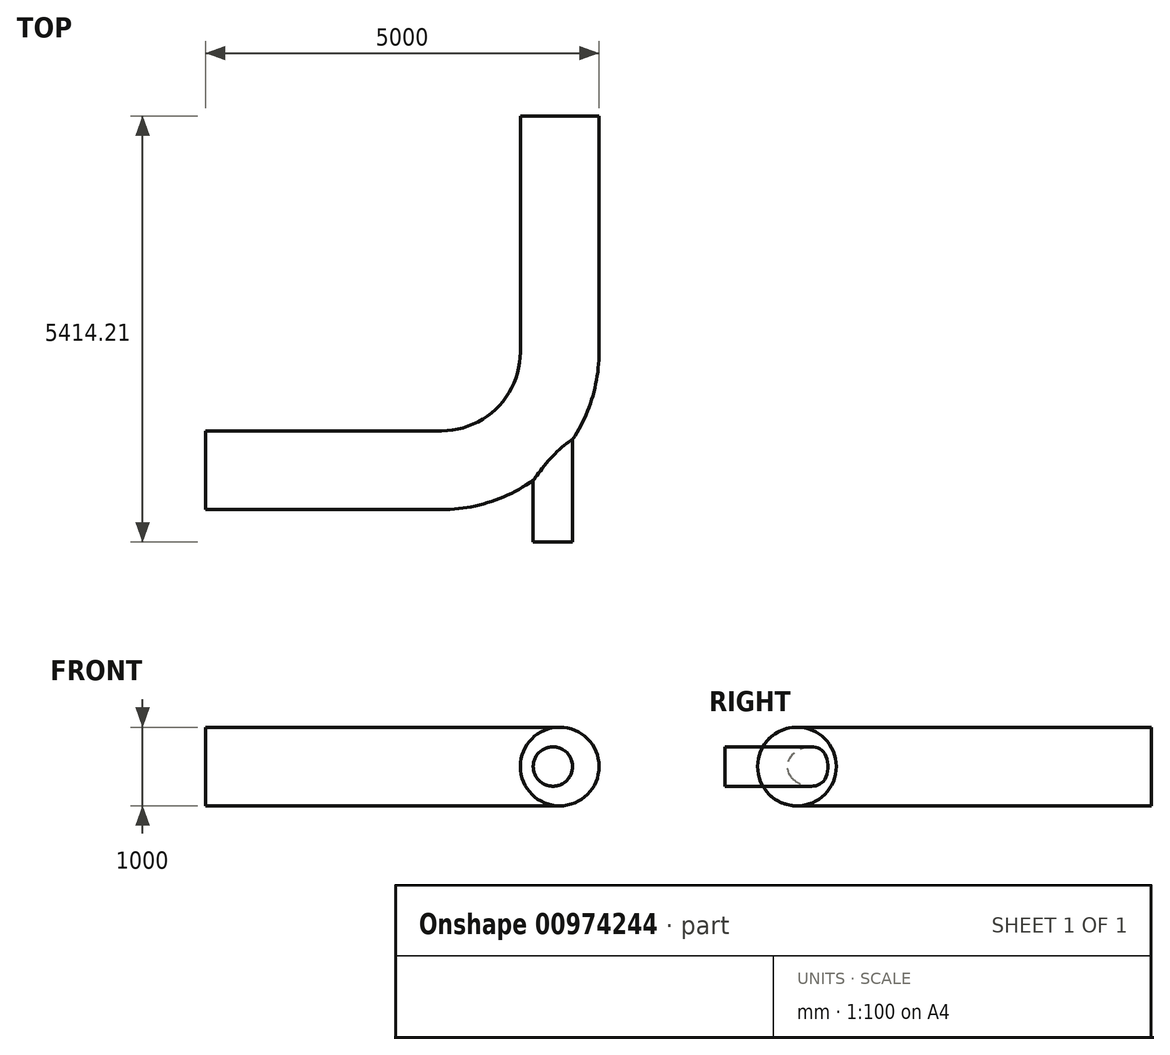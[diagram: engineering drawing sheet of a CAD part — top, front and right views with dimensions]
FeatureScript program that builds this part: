
annotation { "Feature Type Name" : "Feature", "Feature Type Description" : "" }
export const myFeature = defineFeature(function(context is Context, id is Id, definition is map)
    precondition{}
    {
        {
            var Q0;
            Q0=qCreatedBy(makeId("Top.planeOp"),FACE);
            var sketch = newSketch(context, id + "F0", { "sketchPlane" : qUnion([Q0])});
            skLineSegment(sketch, "E0", {"start": v(0, 0) * mm, "end": v(3000, 0) * mm});
            skArc(sketch, "E1", {"start": v(3000, 0) * mm, "mid": v(4060.66, 439.34) * mm, "end": v(4500, 1500) * mm});
            skLineSegment(sketch, "E2", {"start": v(4500, 1500) * mm, "end": v(4500, 4500) * mm});
            skLineSegment(sketch, "E3", {"start": v(3000, 0) * mm, "end": v(3000, 1500) * mm, "construction": true});
            skLineSegment(sketch, "E4", {"start": v(4500, 1500) * mm, "end": v(3000, 1500) * mm, "construction": true});
            skLineSegment(sketch, "E5", {"start": v(3000, 1500) * mm, "end": v(4414.21, 85.79) * mm, "construction": true});
            skLineSegment(sketch, "E6", {"start": v(4414.21, 85.79) * mm, "end": v(4414.21, -914.21) * mm, "construction": true});
            skSolve(sketch);
        }
        {
            var Q0;
            Q0=qCreatedBy(makeId("Right.planeOp"),FACE);
            var sketch = newSketch(context, id + "F1", { "sketchPlane" : qUnion([Q0])});
            skCircle(sketch, "E7", {"center": v(0, 0) * mm, "radius": 500 * mm});
            skSolve(sketch);
        }
        {
            var Q0;
            Q0=makeQuery(id+"F1.imprint","IMPRINT",FACE,{"disambiguationData":[TD([[makeQuery(id+"F1.imprint","IMPRINT",EDGE,{"derivedFrom":sQuery(id+"F1.wireOp",EDGE,"E7")}),1.0]])]});
            var Q1;
            Q1=sQuery(id+"F0.wireOp",EDGE,"E0");
            var Q2;
            Q2=sQuery(id+"F0.wireOp",EDGE,"E1");
            var Q3;
            Q3=sQuery(id+"F0.wireOp",EDGE,"E2");
            sweep(context, id + "F2", {"profiles" : qUnion([Q0]), "path" : qUnion([Q1, Q2, Q3])});
        }
        {
            var Q0;
            Q0=sQuery(id+"F0.wireOp",VERTEX,"E6.end");
            var Q1;
            Q1=sQuery(id+"F0.wireOp",EDGE,"E6");
            cPlane(context, id + "F3", {"entities" : qUnion([Q0, Q1]), "cplaneType" : CPlaneType.LINE_POINT, "offset" : 25 * mm, "width" : 150 * mm, "height" : 150 * mm});
        }
        {
            var Q0;
            Q0=qCreatedBy(id+"F3.planeOp",FACE);
            var sketch = newSketch(context, id + "F4", { "sketchPlane" : qUnion([Q0])});
            skPoint(sketch, "E8.0", {"position": v(4414.21, 0) * mm});
            skCircle(sketch, "E9", {"center": v(4414.21, 0) * mm, "radius": 250 * mm});
            skSolve(sketch);
        }
        {
            var Q0;
            Q0=makeQuery(id+"F4.imprint","IMPRINT",FACE,{"disambiguationData":[TD([[makeQuery(id+"F4.imprint","IMPRINT",EDGE,{"derivedFrom":sQuery(id+"F4.wireOp",EDGE,"E9")}),1.0]])]});
            extrude(context, id + "F5", {"entities" : qUnion([Q0]), "operationType" : NewBodyOperationType.ADD, "oppositeDirection" : true, "depth" : 2212 * mm, "offsetDistance" : 25 * mm});
        }
    });
